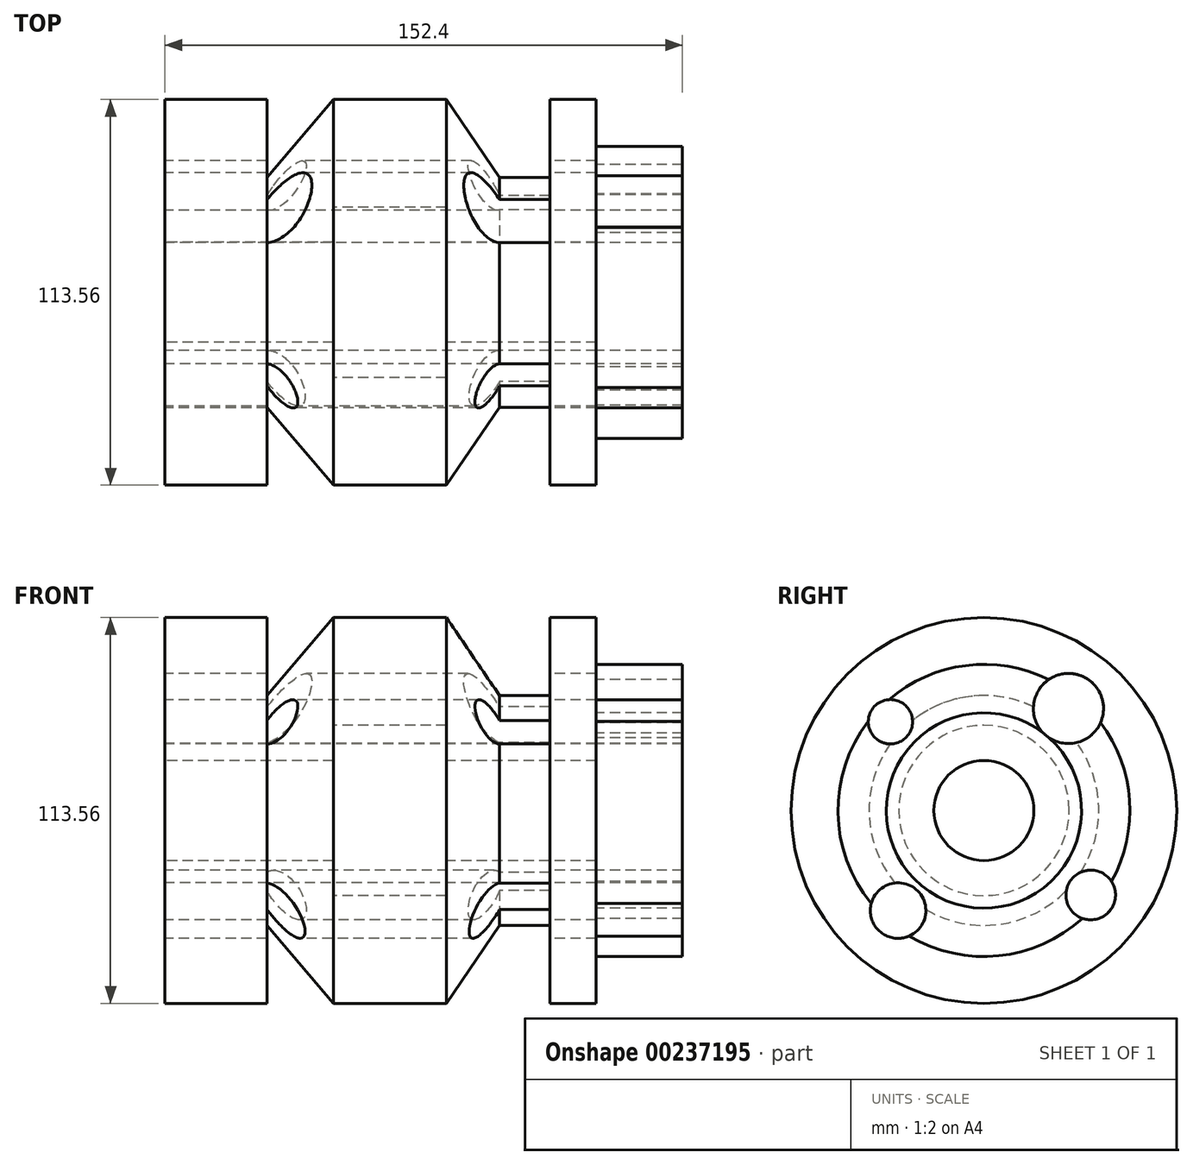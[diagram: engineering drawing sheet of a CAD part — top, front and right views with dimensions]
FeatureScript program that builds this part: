
annotation { "Feature Type Name" : "Feature", "Feature Type Description" : "" }
export const myFeature = defineFeature(function(context is Context, id is Id, definition is map)
    precondition{}
    {
        {
            var Q0;
            Q0=qCreatedBy(makeId("Front.planeOp"),FACE);
            var sketch = newSketch(context, id + "F0", { "sketchPlane" : qUnion([Q0])});
            skLineSegment(sketch, "E0", {"start": v(0, 0) * mm, "end": v(116, 0) * mm, "construction": true});
            skLineSegment(sketch, "E1", {"start": v(0, 14.73) * mm, "end": v(0, 56.78) * mm});
            skLineSegment(sketch, "E2", {"start": v(0, 56.78) * mm, "end": v(30.07, 56.78) * mm});
            skLineSegment(sketch, "E3", {"start": v(30.07, 56.78) * mm, "end": v(30.07, 33.83) * mm});
            skLineSegment(sketch, "E4", {"start": v(30.07, 33.83) * mm, "end": v(49.57, 56.78) * mm});
            skLineSegment(sketch, "E5", {"start": v(49.57, 56.78) * mm, "end": v(82.9, 56.78) * mm});
            skLineSegment(sketch, "E6", {"start": v(82.9, 56.78) * mm, "end": v(98.53, 33.83) * mm});
            skLineSegment(sketch, "E7", {"start": v(98.53, 33.83) * mm, "end": v(113.36, 33.83) * mm});
            skLineSegment(sketch, "E8", {"start": v(113.36, 33.83) * mm, "end": v(113.36, 56.78) * mm});
            skLineSegment(sketch, "E9", {"start": v(113.36, 56.78) * mm, "end": v(127, 56.78) * mm});
            skLineSegment(sketch, "E10", {"start": v(127, 56.78) * mm, "end": v(127, 14.73) * mm});
            skLineSegment(sketch, "E11", {"start": v(127, 14.73) * mm, "end": v(82.9, 14.73) * mm});
            skLineSegment(sketch, "E12", {"start": v(82.9, 14.73) * mm, "end": v(82.9, 25.1) * mm});
            skLineSegment(sketch, "E13", {"start": v(82.9, 25.1) * mm, "end": v(49.57, 25.1) * mm});
            skLineSegment(sketch, "E14", {"start": v(49.57, 25.1) * mm, "end": v(49.57, 14.73) * mm});
            skLineSegment(sketch, "E15", {"start": v(49.57, 14.73) * mm, "end": v(0, 14.73) * mm});
            skPoint(sketch, "E16.orphan", {"position": v(0, 9.45) * mm});
            skSolve(sketch);
        }
        {
            var Q0;
            Q0 = qSketchRegion(id + "F0", true);
            var Q1;
            Q1=sQuery(id+"F0.wireOp",EDGE,"E2");
            var Q2;
            Q2=sQuery(id+"F0.wireOp",EDGE,"E5");
            var Q3;
            Q3=sQuery(id+"F0.wireOp",EDGE,"E4");
            var Q4;
            Q4=sQuery(id+"F0.wireOp",EDGE,"E0");
            revolve(context, id + "F1", {"entities" : qUnion([Q0]), "surfaceEntities" : qUnion([Q1, Q2, Q3]), "axis" : qUnion([Q4]), "revolveType" : RevolveType.FULL});
        }
        {
            var Q0;
            Q0=makeQuery(id+"F1.opRevolve","SWEPT_FACE",FACE,{"disambiguationData":[OSD([sQuery(id+"F0.wireOp",EDGE,"E10")])]});
            var sketch = newSketch(context, id + "F2", { "sketchPlane" : qUnion([Q0])});
            skCircle(sketch, "E17", {"center": v(0, 0) * mm, "radius": 28.76 * mm});
            skCircle(sketch, "E18", {"center": v(0, 0) * mm, "radius": 43 * mm});
            skSolve(sketch);
        }
        {
            var Q0;
            Q0 = qSketchRegion(id + "F2", true);
            extrude(context, id + "F3", {"entities" : qUnion([Q0]), "depth" : 25.4 * mm});
        }
        {
            var Q0;
            Q0=makeQuery(id+"F1.opRevolve","SWEPT_FACE",FACE,{"disambiguationData":[OSD([sQuery(id+"F0.wireOp",EDGE,"E1")])]});
            var sketch = newSketch(context, id + "F4", { "sketchPlane" : qUnion([Q0])});
            skCircle(sketch, "E19", {"center": v(27.54, 26.12) * mm, "radius": 6.52 * mm});
            skCircle(sketch, "E20", {"center": v(25.28, -29.47) * mm, "radius": 8.18 * mm});
            skCircle(sketch, "E21", {"center": v(-31.46, -24.88) * mm, "radius": 7.3 * mm});
            skCircle(sketch, "E22", {"center": v(-24.9, 30.02) * mm, "radius": 10.32 * mm});
            skSolve(sketch);
        }
        {
            var Q0;
            Q0 = qSketchRegion(id + "F4", true);
            extrude(context, id + "F5", {"entities" : qUnion([Q0]), "operationType" : NewBodyOperationType.REMOVE, "endBound" : BoundingType.THROUGH_ALL, "oppositeDirection" : true, "depth" : 25.4 * mm});
        }
    });
